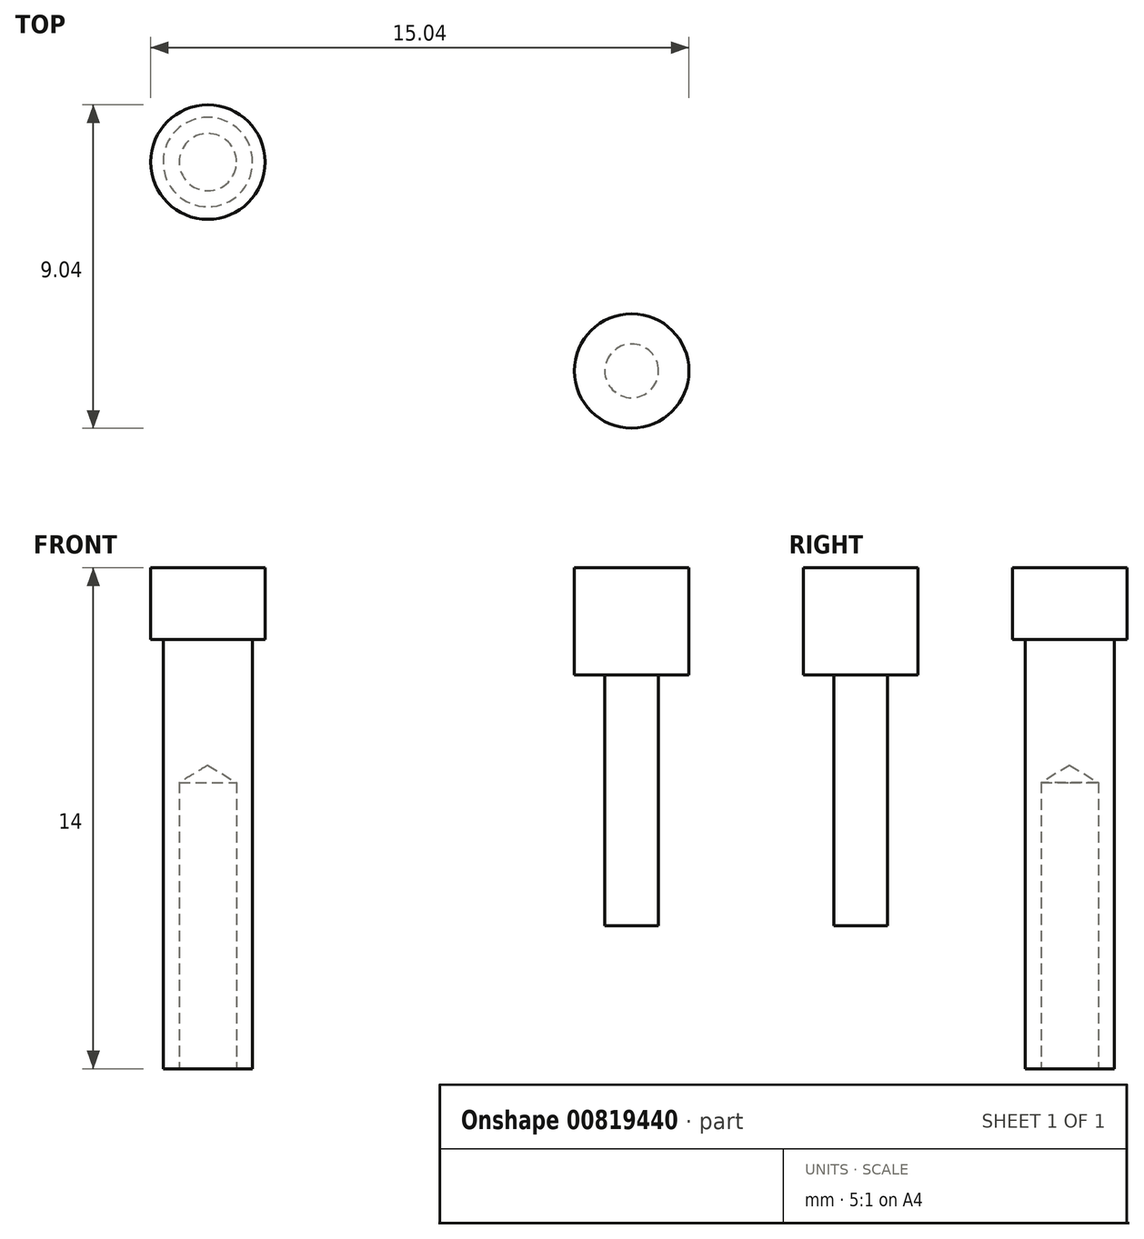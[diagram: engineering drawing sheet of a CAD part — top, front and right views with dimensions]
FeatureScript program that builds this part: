
annotation { "Feature Type Name" : "Feature", "Feature Type Description" : "" }
export const myFeature = defineFeature(function(context is Context, id is Id, definition is map)
    precondition{}
    {
        {
            var Q0;
            Q0=qCreatedBy(makeId("Top.planeOp"),FACE);
            var sketch = newSketch(context, id + "F0", { "sketchPlane" : qUnion([Q0])});
            skCircle(sketch, "E0", {"center": v(0, 0) * mm, "radius": 1.25 * mm});
            skSolve(sketch);
        }
        {
            var Q0;
            Q0 = qSketchRegion(id + "F0", true);
            extrude(context, id + "F1", {"entities" : qUnion([Q0]), "depth" : 12 * mm, "offsetDistance" : 25 * mm});
        }
        {
            var Q0;
            Q0=makeQuery(id+"F1.opExtrude","CAP_FACE",FACE,{"disambiguationData":[OSD([sQuery(id+"F0.wireOp",EDGE,"E0")])],"isStart":false});
            var sketch = newSketch(context, id + "F2", { "sketchPlane" : qUnion([Q0])});
            skCircle(sketch, "E1", {"center": v(0, 0) * mm, "radius": 1.6 * mm});
            skSolve(sketch);
        }
        {
            var Q0;
            Q0 = qSketchRegion(id + "F2", true);
            extrude(context, id + "F3", {"entities" : qUnion([Q0]), "operationType" : NewBodyOperationType.ADD, "depth" : 2 * mm, "offsetDistance" : 25 * mm});
        }
        {
            var Q0;
            Q0=makeQuery(id+"F1.opExtrude","CAP_FACE",FACE,{"disambiguationData":[OSD([sQuery(id+"F0.wireOp",EDGE,"E0")])],"isStart":true});
            var sketch = newSketch(context, id + "F4", { "sketchPlane" : qUnion([Q0])});
            skCircle(sketch, "E2", {"center": v(0, 0) * mm, "radius": 0.75 * mm});
            skSolve(sketch);
        }
        {
            var Q0;
            Q0=sQuery(id+"F4.wireOp",VERTEX,"E2.center");
            var Q1;
            Q1=makeQuery(id+"F1.opExtrude","SWEPT_BODY",BODY,{"disambiguationData":[OSD([sQuery(id+"F0.wireOp",EDGE,"E0")])]});
            hole(context, id + "F5", {"style" : HoleStyle.SIMPLE, "endStyle" : HoleEndStyle.BLIND, "holeDiameter" : 1.6 * mm, "majorDiameter" : 5 * mm, "holeDepth" : 8 * mm, "isTappedThrough" : true, "tappedDepth" : 12 * mm, "tapClearance" : 3, "locations" : qUnion([Q0]), "scope" : qUnion([Q1])});
        }
        {
            var Q0;
            Q0=makeQuery(id+"F3.opExtrude","CAP_FACE",FACE,{"disambiguationData":[OSD([sQuery(id+"F2.wireOp",EDGE,"E1")])],"isStart":false});
            var sketch = newSketch(context, id + "F6", { "sketchPlane" : qUnion([Q0])});
            skCircle(sketch, "E3", {"center": v(11.84, -5.84) * mm, "radius": 1.6 * mm});
            skSolve(sketch);
        }
        {
            var Q0;
            Q0=makeQuery(id+"F6.imprint","IMPRINT",FACE,{"disambiguationData":[TD([[makeQuery(id+"F6.imprint","IMPRINT",EDGE,{"derivedFrom":sQuery(id+"F6.wireOp",EDGE,"E3")}),1.0]])]});
            extrude(context, id + "F7", {"entities" : qUnion([Q0]), "oppositeDirection" : true, "depth" : 3 * mm, "offsetDistance" : 25 * mm});
        }
        {
            var Q0;
            Q0=makeQuery(id+"F7.opExtrude","CAP_FACE",FACE,{"disambiguationData":[OSD([sQuery(id+"F6.wireOp",EDGE,"E3")])],"isStart":false});
            var sketch = newSketch(context, id + "F8", { "sketchPlane" : qUnion([Q0])});
            skCircle(sketch, "E4", {"center": v(11.84, 5.84) * mm, "radius": 0.75 * mm});
            skSolve(sketch);
        }
        {
            var Q0;
            Q0 = qSketchRegion(id + "F8", true);
            extrude(context, id + "F9", {"entities" : qUnion([Q0]), "operationType" : NewBodyOperationType.ADD, "depth" : 7 * mm, "offsetDistance" : 25 * mm});
        }
    });
